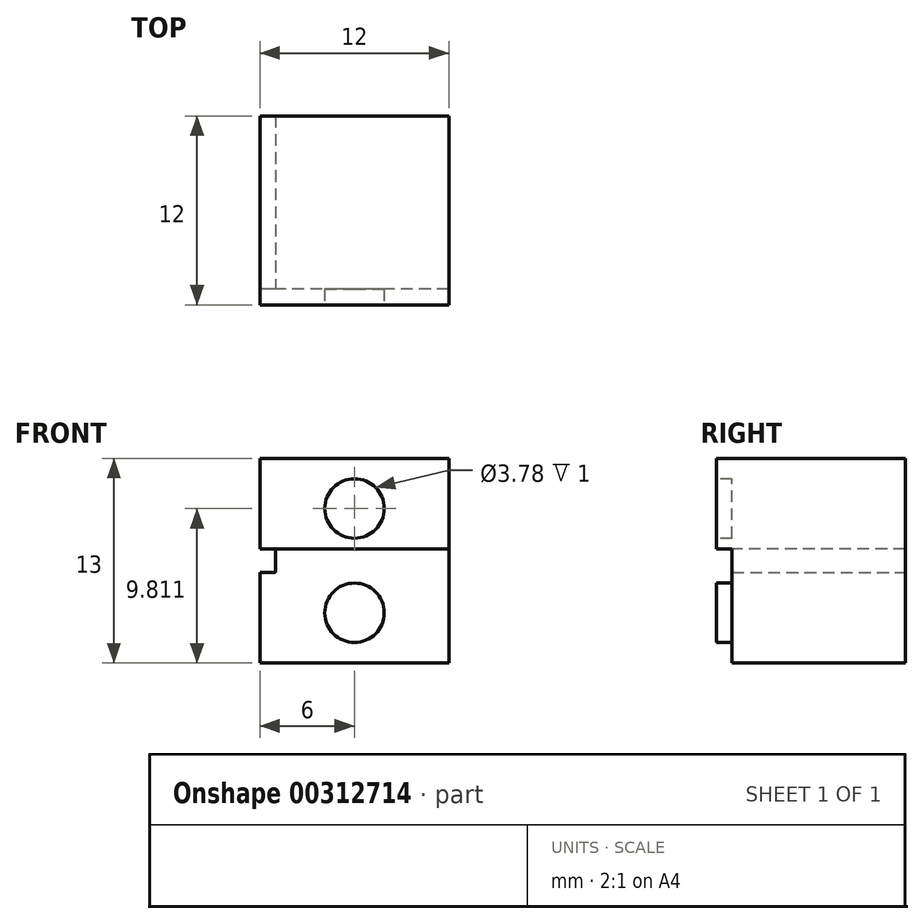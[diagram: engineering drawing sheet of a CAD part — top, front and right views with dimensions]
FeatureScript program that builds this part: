
annotation { "Feature Type Name" : "Feature", "Feature Type Description" : "" }
export const myFeature = defineFeature(function(context is Context, id is Id, definition is map)
    precondition{}
    {
        {
            var Q0;
            Q0=qCreatedBy(makeId("Top.planeOp"),FACE);
            var sketch = newSketch(context, id + "F0", { "sketchPlane" : qUnion([Q0])});
            skLineSegment(sketch, "E0.bottom", {"start": v(6, 6) * mm, "end": v(-6, 6) * mm});
            skLineSegment(sketch, "E0.top", {"start": v(6, -6) * mm, "end": v(-6, -6) * mm});
            skLineSegment(sketch, "E0.left", {"start": v(6, 6) * mm, "end": v(6, -6) * mm});
            skLineSegment(sketch, "E0.right", {"start": v(-6, 6) * mm, "end": v(-6, -6) * mm});
            skPoint(sketch, "E0.middle", {"position": v(0, 0) * mm});
            skSolve(sketch);
        }
        {
            var Q0;
            Q0=makeQuery(id+"F0.imprint","IMPRINT",FACE,{"disambiguationData":[TD([[makeQuery(id+"F0.imprint","IMPRINT",EDGE,{"derivedFrom":sQuery(id+"F0.wireOp",EDGE,"E0.bottom")}),1.0]])]});
            extrude(context, id + "F1", {"entities" : qUnion([Q0]), "depth" : 13 * mm});
        }
        {
            var Q0;
            Q0=makeQuery(id+"F1.opExtrude","SWEPT_FACE",FACE,{"disambiguationData":[OSD([sQuery(id+"F0.wireOp",EDGE,"E0.top")])]});
            var sketch = newSketch(context, id + "F2", { "sketchPlane" : qUnion([Q0])});
            skLineSegment(sketch, "E1.bottom", {"start": v(6, 5.75) * mm, "end": v(-6, 5.75) * mm});
            skLineSegment(sketch, "E1.top", {"start": v(6, 7.25) * mm, "end": v(-6, 7.25) * mm});
            skLineSegment(sketch, "E1.left", {"start": v(6, 5.75) * mm, "end": v(6, 7.25) * mm});
            skLineSegment(sketch, "E1.right", {"start": v(-6, 5.75) * mm, "end": v(-6, 7.25) * mm});
            skPoint(sketch, "E1.middle", {"position": v(0, 6.5) * mm});
            skPoint(sketch, "E1.middle.positionSnap0", {"position": v(-6, 6.5) * mm});
            skPoint(sketch, "E1.centerSnap0", {"position": v(-6, 6.5) * mm});
            skCircle(sketch, "E2", {"center": v(0, 9.81) * mm, "radius": 1.89 * mm});
            skLineSegment(sketch, "E3", {"start": v(-6, 6.5) * mm, "end": v(6, 6.5) * mm, "construction": true});
            skCircle(sketch, "E4.MirrorC", {"center": v(0, 3.19) * mm, "radius": 1.89 * mm});
            skSolve(sketch);
        }
        {
            var Q0;
            Q0=makeQuery(id+"F2.imprint","IMPRINT",FACE,{"disambiguationData":[TD([[makeQuery(id+"F2.imprint","IMPRINT",EDGE,{"derivedFrom":sQuery(id+"F2.wireOp",EDGE,"E1.bottom")}),-1.0]])]});
            var Q1;
            Q1=makeQuery(id+"F2.imprint","IMPRINT",FACE,{"disambiguationData":[TD([[makeQuery(id+"F2.imprint","IMPRINT",EDGE,{"derivedFrom":sQuery(id+"F2.wireOp",EDGE,"E2")}),1.0]])]});
            var Q2;
            Q2=makeQuery(id+"F2.imprint","IMPRINT",FACE,{"disambiguationData":[TD([[makeQuery(id+"F2.imprint","IMPRINT",EDGE,{"derivedFrom":sQuery(id+"F2.wireOp",EDGE,"E4.MirrorC")}),-1.0]])]});
            extrude(context, id + "F3", {"entities" : qUnion([Q0, Q1, Q2]), "operationType" : NewBodyOperationType.REMOVE, "oppositeDirection" : true, "depth" : 1 * mm});
        }
        {
            var Q0;
            Q0=makeQuery(id+"F1.opExtrude","SWEPT_FACE",FACE,{"disambiguationData":[OSD([sQuery(id+"F0.wireOp",EDGE,"E0.right")])]});
            var sketch = newSketch(context, id + "F4", { "sketchPlane" : qUnion([Q0])});
            skLineSegment(sketch, "E5.bottom", {"start": v(6, 7.25) * mm, "end": v(-6, 7.25) * mm});
            skLineSegment(sketch, "E5.top", {"start": v(6, 5.75) * mm, "end": v(-6, 5.75) * mm});
            skLineSegment(sketch, "E5.left", {"start": v(6, 7.25) * mm, "end": v(6, 5.75) * mm});
            skLineSegment(sketch, "E5.right", {"start": v(-6, 7.25) * mm, "end": v(-6, 5.75) * mm});
            skSolve(sketch);
        }
        {
            var Q0;
            Q0 = qSketchRegion(id + "F4", true);
            extrude(context, id + "F5", {"entities" : qUnion([Q0]), "operationType" : NewBodyOperationType.REMOVE, "oppositeDirection" : true, "depth" : 1 * mm});
        }
    });
